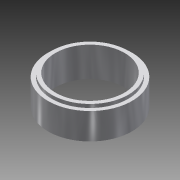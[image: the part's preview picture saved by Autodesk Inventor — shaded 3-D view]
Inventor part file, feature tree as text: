
AUTODESK INVENTOR PART (.ipt)
format: ipt  version: 2015 (Build 190159000, 159)  size: 123,904 bytes
history: native  units: in
note: dims shown in document units (in); Inventor stores cm internally (conversion verified against a paired STEP export)
features: revolve x1, sketch x1
ambient origin geometry x8: Origin, YZ Plane, XZ Plane, XY Plane, X Axis, Y Axis, Z Axis, Center Point
bodies: Solid1 (feature_tree)
feature tree (2):
  revolve  "Revolution1"  [1 undecoded]
  sketch  "Sketch1"  dims[d0=0.75in d1=1.0in d2=0.2185in d3=2.594in d4=0.5841in d5=0.5in d6=1.844in d7=0.5in d8=1.75in d9=0.25in d10=105.0deg d11=0.5in d12=0.5in d13=0.25in d14=0.375in d15=2.0in d16=0.5in d17=0.25in d18=0.234in d19=0.25in d20=2.0in d21=0.25in d22=105.0deg d23=0.125in d24=0.25in d25=2.3995in d26=0.125in d27=0.25in d28=180.0deg]
note: 1 required parameter value undecoded (feature->parameter linkage not recoverable at this tier; creation-order binding heuristic only, values carry confidence <= 0.55)
